# Revit family: EKF_EE_МонтажнаяПанельГлухаяTrivia_AVERES
name_source: partatom
category: Электрооборудование
units: mm (PartAtom-declared; Revit-internal decimal feet)

## family parameters
Всегда вертикально = Нет
На основе рабочей плоскости = Да
Общий = Да
При загрузке вырезать с полостями = Нет
Размер круглого соединителя = Использовать диаметр
Тип детали = Силовой щит
Точка расчета площади = Нет

## types (12) — shared parameters
ADSK_Единица измерения = шт.
ADSK_Завод-изготовитель = EKF
ADSK_Количество = 1
ADSK_Материал = RAL 7035_Сталь
ADSK_Размер_Глубина = 27 мм
Глубина = 400 мм
Изготовитель = EKF
МПГ = Да
Отметка по умолчанию = 1219.2 мм
Серия номенклатуры = Averes
Степень защиты IP = -
ТВ = EKF_2_TRIVIA_AVERES
Тип установки = -
Тип_Панели = Вл_Монтажная панель
zero-valued in all types: ADSK_Масса

## per-type parameters (varying)
| type | ADSK_Код изделия | ADSK_Размер_Высота | ADSK_Размер_Ширина | Тип |
| Монтажная панель В300 Ш300 глухая EKF AVERES | MP3M300 | 300 мм | 200 мм | 507 мм |
| Монтажная панель В300 Ш400 глухая EKF AVERES | MP3M400 | 300 мм | 300 мм | 509 мм |
| Монтажная панель В300 Ш600 глухая EKF AVERES | MP3M600 | 300 мм | 500 мм | 511 мм |
| Монтажная панель В300 Ш800 глухая EKF AVERES | MP3M800 | 300 мм | 700 мм | 513 мм |
| Монтажная панель В600 Ш300 глухая EKF AVERES | MP6M300 | 600 мм | 200 мм | 515 мм |
| Монтажная панель В600 Ш400 глухая EKF AVERES | MP6M400 | 600 мм | 300 мм | 517 мм |
| Монтажная панель В600 Ш600 глухая EKF AVERES | MP6M600 | 600 мм | 500 мм | 519 мм |
| Монтажная панель В600 Ш800 глухая EKF AVERES | MP6M800 | 600 мм | 700 мм | 521 мм |
| Монтажная панель В900 Ш300 глухая EKF AVERES | MP9M300 | 1015 мм | 200 мм | 523 мм |
| Монтажная панель В900 Ш400 глухая EKF AVERES | MP9M400 | 1015 мм | 300 мм | 525 мм |
| Монтажная панель В900 Ш600 глухая EKF AVERES | MP9M600 | 1015 мм | 500 мм | 527 мм |
| Монтажная панель В900 Ш800 глухая EKF AVERES | MP9M800 | 1015 мм | 700 мм | 529 мм |

note: column(s) folded — value = type name in every type: ADSK_Марка, ADSK_Наименование, ADSK_Обозначение
